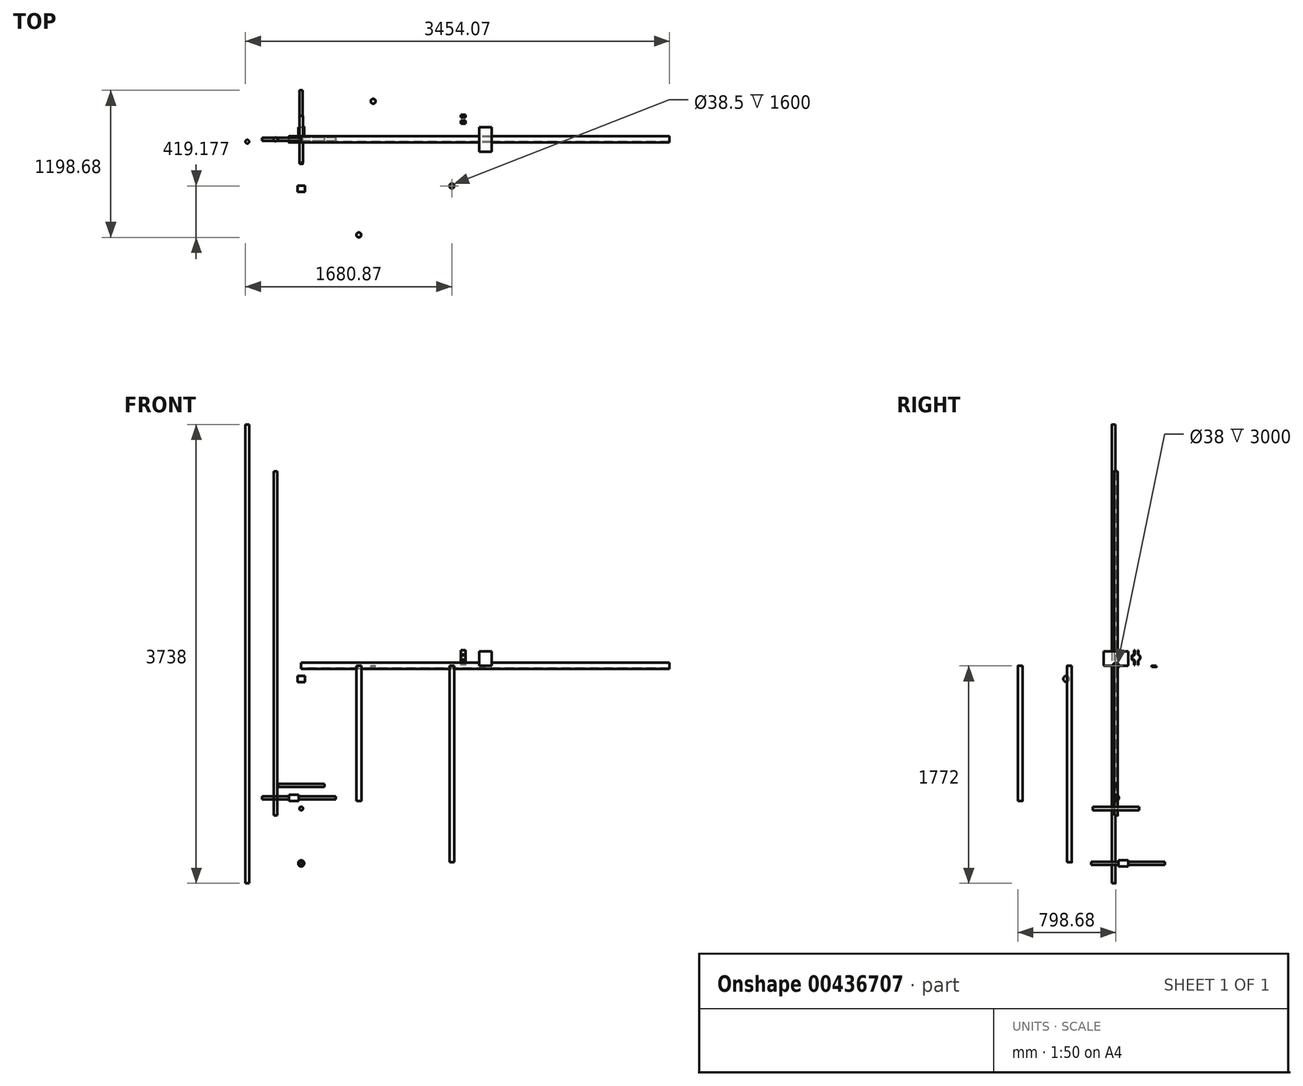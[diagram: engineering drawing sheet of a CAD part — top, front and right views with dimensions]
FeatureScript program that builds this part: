
annotation { "Feature Type Name" : "Feature", "Feature Type Description" : "" }
export const myFeature = defineFeature(function(context is Context, id is Id, definition is map)
    precondition{}
    {
        {
            var Q0;
            Q0=qCreatedBy(makeId("Right.planeOp"),FACE);
            var sketch = newSketch(context, id + "F0", { "sketchPlane" : qUnion([Q0])});
            skCircle(sketch, "E0", {"center": v(0, 0) * mm, "radius": 25 * mm});
            skCircle(sketch, "E1", {"center": v(0, 0) * mm, "radius": 19 * mm});
            skSolve(sketch);
        }
        {
            var Q0;
            Q0 = qSketchRegion(id + "F0", true);
            extrude(context, id + "F1", {"entities" : qUnion([Q0]), "depth" : 3000 * mm});
        }
        {
            var Q0;
            Q0=qCreatedBy(makeId("Right.planeOp"),FACE);
            cPlane(context, id + "F2", {"entities" : qUnion([Q0]), "cplaneType" : CPlaneType.OFFSET, "offset" : 1500 * mm, "width" : 150 * mm, "height" : 150 * mm});
        }
        {
            var Q0;
            Q0=qCreatedBy(id+"F2.planeOp",FACE);
            var sketch = newSketch(context, id + "F3", { "sketchPlane" : qUnion([Q0])});
            skLineSegment(sketch, "E2.top", {"start": v(-100, 0) * mm, "end": v(100, 0) * mm});
            skPoint(sketch, "E2.middle", {"position": v(0, 0) * mm});
            skLineSegment(sketch, "E3.MirrorCS", {"start": v(-100, 118.56) * mm, "end": v(100, 118.56) * mm});
            skLineSegment(sketch, "E4.MirrorCS", {"start": v(-100, 118.56) * mm, "end": v(-100, 0) * mm});
            skLineSegment(sketch, "E5.MirrorCS", {"start": v(100, 118.56) * mm, "end": v(100, 0) * mm});
            skSolve(sketch);
        }
        {
            var Q0;
            Q0 = qSketchRegion(id + "F3", true);
            extrude(context, id + "F4", {"entities" : qUnion([Q0]), "operationType" : NewBodyOperationType.ADD, "depth" : 50 * mm, "hasSecondDirection" : true, "secondDirectionOppositeDirection" : true, "secondDirectionDepth" : 50 * mm});
        }
        {
            var Q0;
            Q0=qCreatedBy(makeId("Top.planeOp"),FACE);
            var sketch = newSketch(context, id + "F5", { "sketchPlane" : qUnion([Q0])});
            skCircle(sketch, "E6", {"center": v(-439.07, -18.7) * mm, "radius": 15 * mm});
            skSolve(sketch);
        }
        {
            var Q0;
            Q0 = qSketchRegion(id + "F5", true);
            extrude(context, id + "F6", {"entities" : qUnion([Q0]), "depth" : 1966 * mm, "hasSecondDirection" : true, "secondDirectionOppositeDirection" : true, "secondDirectionDepth" : 1772 * mm});
        }
        {
            var Q0;
            Q0=qCreatedBy(makeId("Top.planeOp"),FACE);
            cPlane(context, id + "F7", {"entities" : qUnion([Q0]), "cplaneType" : CPlaneType.OFFSET, "offset" : 1609 * mm, "oppositeDirection" : true, "width" : 150 * mm, "height" : 150 * mm});
        }
        {
            var Q0;
            Q0=qCreatedBy(makeId("Front.planeOp"),FACE);
            var sketch = newSketch(context, id + "F8", { "sketchPlane" : qUnion([Q0])});
            skCircle(sketch, "E7", {"center": v(0, -1609) * mm, "radius": 25 * mm});
            skSolve(sketch);
        }
        {
            var Q0;
            Q0 = qSketchRegion(id + "F8", true);
            extrude(context, id + "F9", {"entities" : qUnion([Q0]), "oppositeDirection" : true, "depth" : 100 * mm, "hasSecondDirection" : true, "secondDirectionOppositeDirection" : true, "secondDirectionDepth" : 20 * mm});
        }
        {
            var Q0;
            Q0=makeQuery(id+"F9.opExtrude","CAP_FACE",FACE,{"disambiguationData":[OSD([sQuery(id+"F8.wireOp",EDGE,"E7")])],"isStart":false});
            var sketch = newSketch(context, id + "F10", { "sketchPlane" : qUnion([Q0])});
            skCircle(sketch, "E8", {"center": v(0, -1609) * mm, "radius": 12.5 * mm});
            skSolve(sketch);
        }
        {
            var Q0;
            Q0 = qSketchRegion(id + "F10", true);
            extrude(context, id + "F11", {"entities" : qUnion([Q0]), "operationType" : NewBodyOperationType.ADD, "depth" : 300 * mm, "hasSecondDirection" : true, "secondDirectionOppositeDirection" : true, "secondDirectionDepth" : 300 * mm});
        }
        {
            var Q0;
            Q0=qCreatedBy(makeId("Top.planeOp"),FACE);
            cPlane(context, id + "F12", {"entities" : qUnion([Q0]), "cplaneType" : CPlaneType.OFFSET, "offset" : 1075 * mm, "oppositeDirection" : true, "width" : 150 * mm, "height" : 150 * mm});
        }
        {
            var Q0;
            Q0=qCreatedBy(makeId("Right.planeOp"),FACE);
            var sketch = newSketch(context, id + "F13", { "sketchPlane" : qUnion([Q0])});
            skCircle(sketch, "E9", {"center": v(0, -1075) * mm, "radius": 25 * mm});
            skSolve(sketch);
        }
        {
            var Q0;
            Q0 = qSketchRegion(id + "F13", true);
            var Q1;
            Q1=sQuery(id+"F13.wireOp",EDGE,"E9");
            extrude(context, id + "F14", {"entities" : qUnion([Q0]), "surfaceEntities" : qUnion([Q1]), "oppositeDirection" : true, "depth" : 100 * mm, "hasSecondDirection" : true, "secondDirectionOppositeDirection" : true, "secondDirectionDepth" : 20 * mm});
        }
        {
            var Q0;
            Q0=makeQuery(id+"F14.opExtrude","CAP_FACE",FACE,{"disambiguationData":[OSD([sQuery(id+"F13.wireOp",EDGE,"E9")])],"isStart":true});
            var sketch = newSketch(context, id + "F15", { "sketchPlane" : qUnion([Q0])});
            skCircle(sketch, "E10", {"center": v(0, -1075) * mm, "radius": 12.5 * mm});
            skSolve(sketch);
        }
        {
            var Q0;
            Q0 = qSketchRegion(id + "F15", true);
            extrude(context, id + "F16", {"entities" : qUnion([Q0]), "operationType" : NewBodyOperationType.ADD, "depth" : 300 * mm, "hasSecondDirection" : true, "secondDirectionOppositeDirection" : true, "secondDirectionDepth" : 300 * mm});
        }
        {
            var Q0;
            Q0=qCreatedBy(makeId("Right.planeOp"),FACE);
            cPlane(context, id + "F17", {"entities" : qUnion([Q0]), "cplaneType" : CPlaneType.OFFSET, "offset" : 1300 * mm, "width" : 150 * mm, "height" : 150 * mm});
        }
        {
            var Q0;
            Q0=qCreatedBy(id+"F17.planeOp",FACE);
            var sketch = newSketch(context, id + "F18", { "sketchPlane" : qUnion([Q0])});
            skLineSegment(sketch, "E11", {"start": v(184.47, 6.62) * mm, "end": v(184.47, 41.62) * mm});
            skLineSegment(sketch, "E12", {"start": v(184.47, 41.62) * mm, "end": v(199.47, 56.62) * mm});
            skLineSegment(sketch, "E13", {"start": v(199.47, 56.62) * mm, "end": v(199.47, 78.62) * mm});
            skLineSegment(sketch, "E14", {"start": v(184.47, 128.62) * mm, "end": v(179.47, 128.62) * mm});
            skLineSegment(sketch, "E15", {"start": v(179.47, 128.62) * mm, "end": v(179.47, 93.69) * mm});
            skLineSegment(sketch, "E16", {"start": v(179.47, 93.69) * mm, "end": v(194.47, 78.69) * mm});
            skLineSegment(sketch, "E17", {"start": v(194.47, 78.69) * mm, "end": v(194.47, 56.62) * mm});
            skLineSegment(sketch, "E18", {"start": v(194.47, 56.62) * mm, "end": v(179.47, 41.62) * mm});
            skLineSegment(sketch, "E19", {"start": v(179.47, 41.62) * mm, "end": v(179.47, 6.62) * mm});
            skLineSegment(sketch, "E20", {"start": v(179.47, 6.62) * mm, "end": v(184.47, 6.62) * mm});
            skLineSegment(sketch, "E21", {"start": v(184.47, 128.62) * mm, "end": v(184.47, 93.62) * mm});
            skLineSegment(sketch, "E22", {"start": v(184.47, 93.62) * mm, "end": v(199.47, 78.62) * mm});
            skLineSegment(sketch, "E23", {"start": v(154.39, 93.62) * mm, "end": v(154.39, 128.62) * mm});
            skLineSegment(sketch, "E24", {"start": v(154.39, 128.62) * mm, "end": v(149.39, 128.62) * mm});
            skLineSegment(sketch, "E25", {"start": v(149.39, 128.62) * mm, "end": v(149.39, 93.62) * mm});
            skLineSegment(sketch, "E26", {"start": v(154.39, 41.62) * mm, "end": v(154.39, 6.62) * mm});
            skLineSegment(sketch, "E27", {"start": v(154.39, 6.62) * mm, "end": v(149.39, 6.62) * mm});
            skLineSegment(sketch, "E28", {"start": v(149.39, 6.62) * mm, "end": v(149.39, 41.62) * mm});
            skLineSegment(sketch, "E29", {"start": v(119.25, 133.62) * mm, "end": v(221.84, 133.62) * mm, "construction": true});
            skLineSegment(sketch, "E30", {"start": v(142.52, 81.62) * mm, "end": v(133.39, 81.62) * mm});
            skLineSegment(sketch, "E31", {"start": v(133.39, 81.62) * mm, "end": v(133.39, 53.62) * mm});
            skLineSegment(sketch, "E32", {"start": v(133.39, 53.62) * mm, "end": v(142.52, 53.62) * mm});
            skLineSegment(sketch, "E33", {"start": v(142.46, 48.62) * mm, "end": v(128.39, 48.62) * mm});
            skLineSegment(sketch, "E34", {"start": v(128.39, 48.62) * mm, "end": v(128.39, 86.62) * mm});
            skLineSegment(sketch, "E35", {"start": v(128.39, 86.62) * mm, "end": v(142.46, 86.62) * mm});
            skLineSegment(sketch, "E36", {"start": v(149.39, 93.62) * mm, "end": v(142.46, 86.62) * mm});
            skLineSegment(sketch, "E37", {"start": v(149.39, 41.62) * mm, "end": v(142.46, 48.62) * mm});
            skLineSegment(sketch, "E38", {"start": v(142.52, 53.62) * mm, "end": v(154.39, 41.62) * mm});
            skLineSegment(sketch, "E39", {"start": v(154.39, 93.62) * mm, "end": v(142.52, 81.62) * mm});
            skCircle(sketch, "E40", {"center": v(167.22, 67.86) * mm, "radius": 25 * mm, "construction": true});
            skSolve(sketch);
        }
        {
            var Q0;
            Q0 = qSketchRegion(id + "F18", true);
            extrude(context, id + "F19", {"entities" : qUnion([Q0]), "depth" : 40 * mm});
        }
        {
            var Q0;
            Q0=qCreatedBy(makeId("Top.planeOp"),FACE);
            var sketch = newSketch(context, id + "F20", { "sketchPlane" : qUnion([Q0])});
            skCircle(sketch, "E41", {"center": v(1226.8, -379.5) * mm, "radius": 20 * mm});
            skCircle(sketch, "E42", {"center": v(1226.8, -379.5) * mm, "radius": 19.25 * mm});
            skSolve(sketch);
        }
        {
            var Q0;
            Q0 = qSketchRegion(id + "F20", true);
            extrude(context, id + "F21", {"entities" : qUnion([Q0]), "oppositeDirection" : true, "depth" : 1600 * mm});
        }
        {
            var Q0;
            Q0=qCreatedBy(makeId("Top.planeOp"),FACE);
            var sketch = newSketch(context, id + "F22", { "sketchPlane" : qUnion([Q0])});
            skCircle(sketch, "E43", {"center": v(-210.03, 0) * mm, "radius": 15 * mm});
            skSolve(sketch);
        }
        {
            var Q0;
            Q0 = qSketchRegion(id + "F22", true);
            extrude(context, id + "F23", {"entities" : qUnion([Q0]), "depth" : 1586 * mm, "hasSecondDirection" : true, "secondDirectionOppositeDirection" : true, "secondDirectionDepth" : 1219 * mm});
        }
        {
            var Q0;
            Q0=qCreatedBy(makeId("Top.planeOp"),FACE);
            cPlane(context, id + "F24", {"entities" : qUnion([Q0]), "cplaneType" : CPlaneType.OFFSET, "offset" : 975 * mm, "oppositeDirection" : true, "width" : 150 * mm, "height" : 150 * mm});
        }
        {
            var Q0;
            Q0=qCreatedBy(makeId("Right.planeOp"),FACE);
            var sketch = newSketch(context, id + "F25", { "sketchPlane" : qUnion([Q0])});
            skCircle(sketch, "E44", {"center": v(0, -975) * mm, "radius": 12.5 * mm});
            skSolve(sketch);
        }
        {
            var Q0;
            Q0 = qSketchRegion(id + "F25", true);
            extrude(context, id + "F26", {"entities" : qUnion([Q0]), "operationType" : NewBodyOperationType.ADD, "depth" : 190 * mm, "hasSecondDirection" : true, "secondDirectionOppositeDirection" : true, "secondDirectionDepth" : 190 * mm});
        }
        {
            var Q0;
            Q0=qCreatedBy(makeId("Top.planeOp"),FACE);
            cPlane(context, id + "F27", {"entities" : qUnion([Q0]), "cplaneType" : CPlaneType.OFFSET, "offset" : 1162 * mm, "oppositeDirection" : true, "width" : 150 * mm, "height" : 150 * mm});
        }
        {
            var Q0;
            Q0=qCreatedBy(makeId("Front.planeOp"),FACE);
            var sketch = newSketch(context, id + "F28", { "sketchPlane" : qUnion([Q0])});
            skCircle(sketch, "E45", {"center": v(0, -1162) * mm, "radius": 15 * mm});
            skSolve(sketch);
        }
        {
            var Q0;
            Q0 = qSketchRegion(id + "F28", true);
            extrude(context, id + "F29", {"entities" : qUnion([Q0]), "operationType" : NewBodyOperationType.ADD, "depth" : 190 * mm, "hasSecondDirection" : true, "secondDirectionOppositeDirection" : true, "secondDirectionDepth" : 190 * mm});
        }
        {
            var Q0;
            Q0=qCreatedBy(makeId("Right.planeOp"),FACE);
            var sketch = newSketch(context, id + "F30", { "sketchPlane" : qUnion([Q0])});
            skCircle(sketch, "E46", {"center": v(-403.54, -106.75) * mm, "radius": 25 * mm});
            skSolve(sketch);
        }
        {
            var Q0;
            Q0=makeQuery(id+"F30.imprint","IMPRINT",FACE,{"disambiguationData":[TD([[makeQuery(id+"F30.imprint","IMPRINT",EDGE,{"derivedFrom":sQuery(id+"F30.wireOp",EDGE,"E46")}),1.0]])]});
            var Q1;
            Q1=sQuery(id+"F30.wireOp",EDGE,"E46");
            extrude(context, id + "F31", {"entities" : qUnion([Q0]), "surfaceEntities" : qUnion([Q1]), "depth" : 30 * mm, "hasSecondDirection" : true, "secondDirectionOppositeDirection" : true, "secondDirectionDepth" : 30 * mm});
        }
        {
            var Q0;
            Q0=qCreatedBy(makeId("Top.planeOp"),FACE);
            var sketch = newSketch(context, id + "F32", { "sketchPlane" : qUnion([Q0])});
            skCircle(sketch, "E47", {"center": v(469.3, -778.68) * mm, "radius": 20 * mm});
            skCircle(sketch, "E48", {"center": v(469.3, -778.68) * mm, "radius": 19.25 * mm});
            skSolve(sketch);
        }
        {
            var Q0;
            Q0 = qSketchRegion(id + "F32", true);
            extrude(context, id + "F33", {"entities" : qUnion([Q0]), "oppositeDirection" : true, "depth" : 1100 * mm});
        }
        {
            var Q0;
            Q0=qCreatedBy(makeId("Top.planeOp"),FACE);
            var sketch = newSketch(context, id + "F34", { "sketchPlane" : qUnion([Q0])});
            skCircle(sketch, "E49", {"center": v(586.2, 310.23) * mm, "radius": 20 * mm});
            skCircle(sketch, "E50", {"center": v(586.2, 310.23) * mm, "radius": 19.25 * mm});
            skSolve(sketch);
        }
        {
            var Q0;
            Q0 = qSketchRegion(id + "F34", true);
            extrude(context, id + "F35", {"entities" : qUnion([Q0]), "oppositeDirection" : true, "depth" : 10 * mm});
        }
    });
